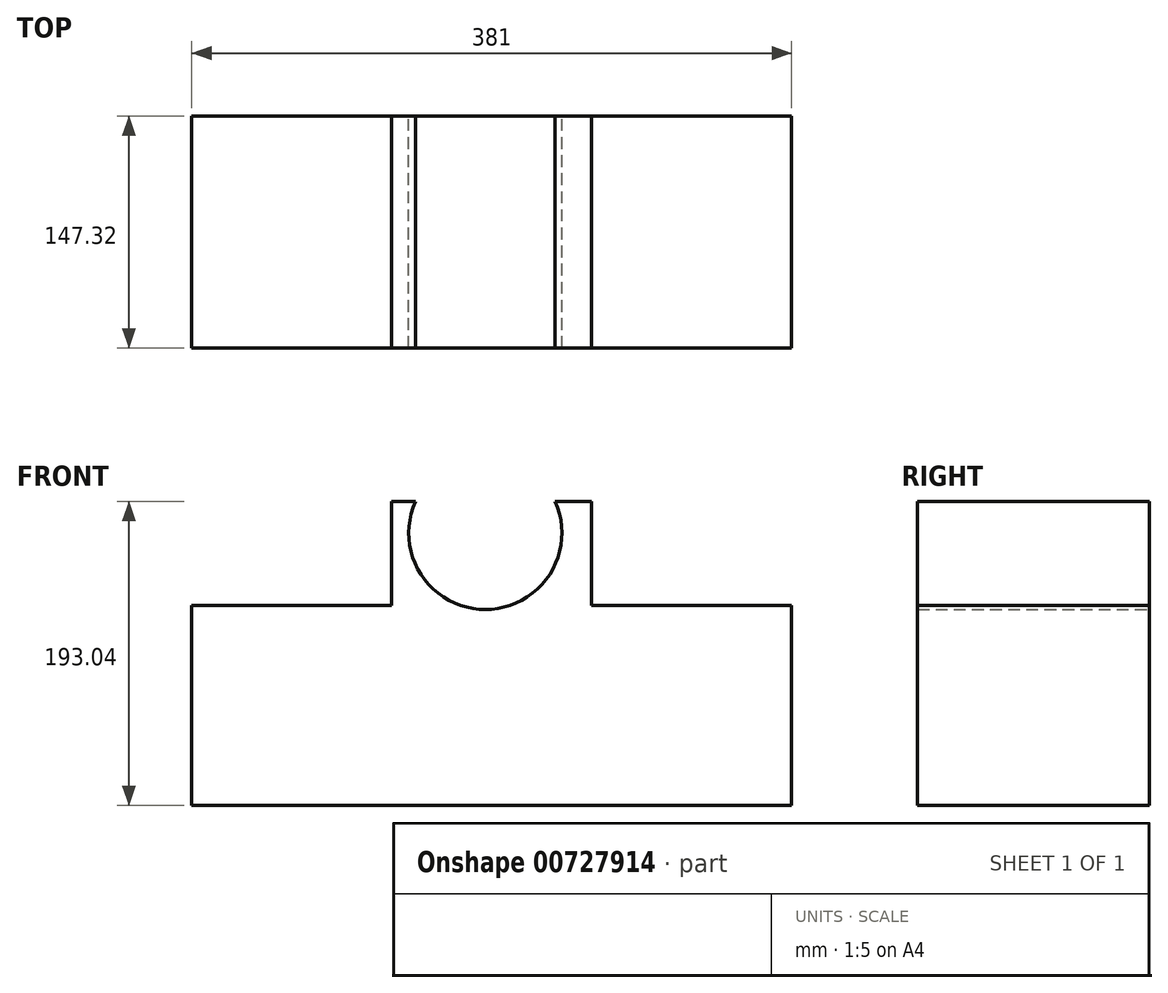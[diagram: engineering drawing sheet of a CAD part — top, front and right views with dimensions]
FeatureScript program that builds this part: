
annotation { "Feature Type Name" : "Feature", "Feature Type Description" : "" }
export const myFeature = defineFeature(function(context is Context, id is Id, definition is map)
    precondition{}
    {
        {
            var Q0;
            Q0=qCreatedBy(makeId("Front.planeOp"),FACE);
            var sketch = newSketch(context, id + "F0", { "sketchPlane" : qUnion([Q0])});
            skLineSegment(sketch, "E0", {"start": v(-29.11, -24.86) * mm, "end": v(351.89, -24.86) * mm});
            skLineSegment(sketch, "E1", {"start": v(-29.11, -24.86) * mm, "end": v(-29.11, 102.14) * mm});
            skLineSegment(sketch, "E2", {"start": v(-29.11, 102.14) * mm, "end": v(97.89, 102.14) * mm});
            skLineSegment(sketch, "E3", {"start": v(351.89, -24.86) * mm, "end": v(351.89, 102.14) * mm});
            skLineSegment(sketch, "E4", {"start": v(351.89, 102.14) * mm, "end": v(224.89, 102.14) * mm});
            skLineSegment(sketch, "E5", {"start": v(97.89, 102.14) * mm, "end": v(97.89, 168.18) * mm});
            skLineSegment(sketch, "E6", {"start": v(224.89, 102.14) * mm, "end": v(224.89, 168.18) * mm});
            skArc(sketch, "E7", {"start": v(112.94, 168.18) * mm, "mid": v(157.32, 99.6) * mm, "end": v(201.7, 168.18) * mm});
            skLineSegment(sketch, "E8", {"start": v(97.89, 168.18) * mm, "end": v(112.94, 168.18) * mm});
            skLineSegment(sketch, "E9", {"start": v(201.7, 168.18) * mm, "end": v(224.89, 168.18) * mm});
            skSolve(sketch);
        }
        {
            var Q0;
            Q0=makeQuery(id+"F0.imprint","IMPRINT",FACE,{"disambiguationData":[TD([[makeQuery(id+"F0.imprint","IMPRINT",EDGE,{"derivedFrom":sQuery(id+"F0.wireOp",EDGE,"E0")}),1.0]])]});
            extrude(context, id + "F1", {"entities" : qUnion([Q0]), "depth" : 147.32 * mm, "offsetDistance" : 25.4 * mm});
        }
    });
